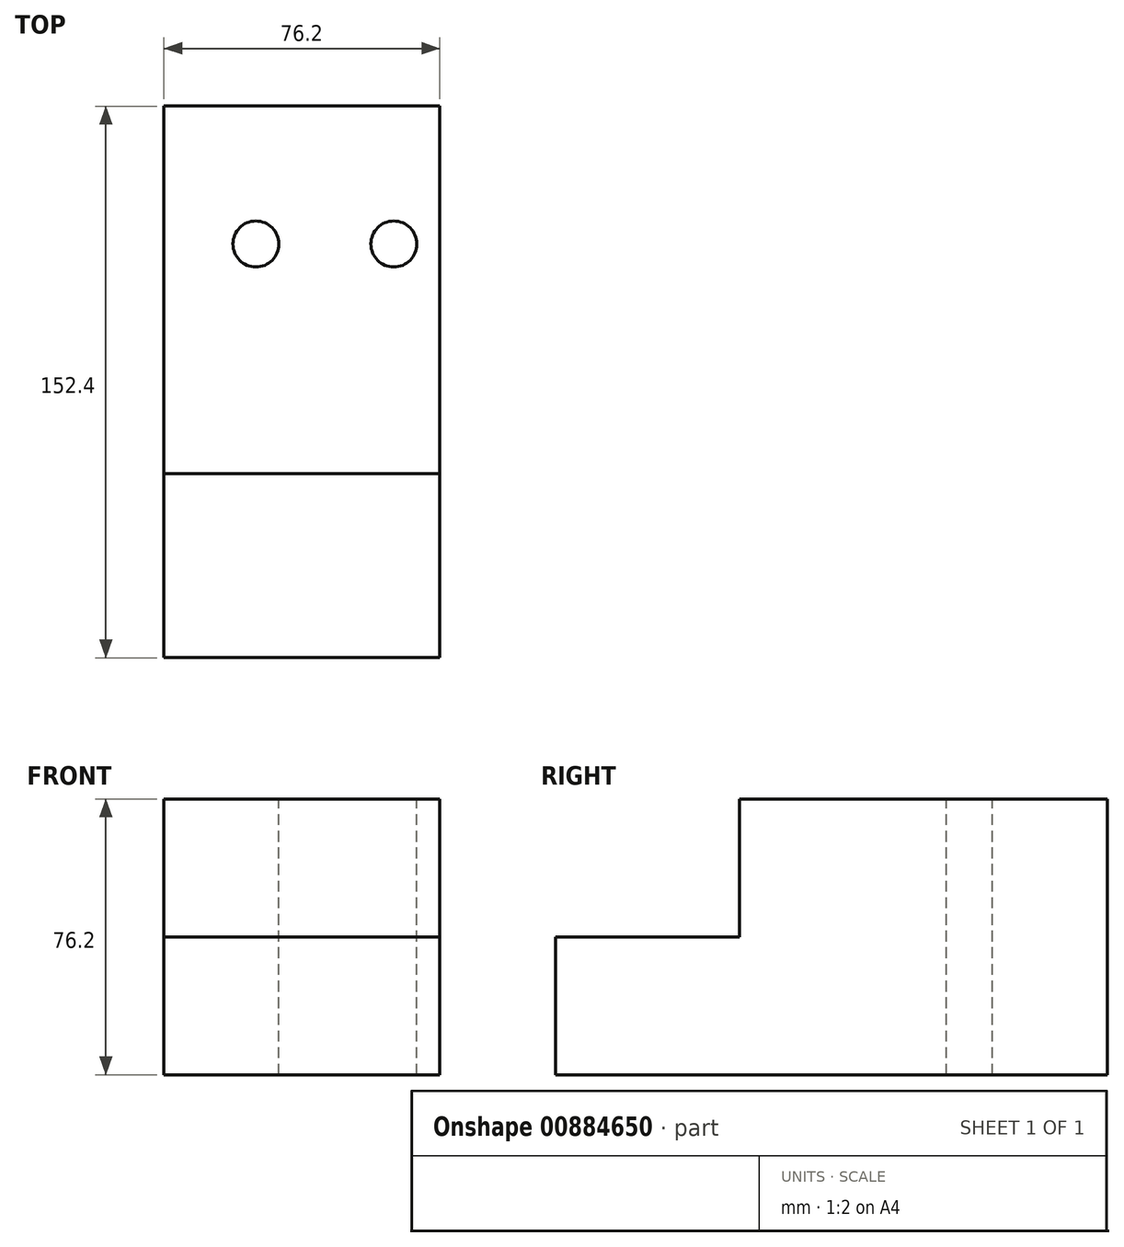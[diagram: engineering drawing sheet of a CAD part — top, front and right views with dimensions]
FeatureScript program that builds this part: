
annotation { "Feature Type Name" : "Feature", "Feature Type Description" : "" }
export const myFeature = defineFeature(function(context is Context, id is Id, definition is map)
    precondition{}
    {
        {
            var Q0;
            Q0=qCreatedBy(makeId("Top.planeOp"),FACE);
            var sketch = newSketch(context, id + "F0", { "sketchPlane" : qUnion([Q0])});
            skLineSegment(sketch, "E0.bottom", {"start": v(-31.3, 38.55) * mm, "end": v(44.9, 38.55) * mm});
            skLineSegment(sketch, "E0.top", {"start": v(-31.3, -63.05) * mm, "end": v(44.9, -63.05) * mm});
            skLineSegment(sketch, "E0.left", {"start": v(-31.3, 38.55) * mm, "end": v(-31.3, -63.05) * mm});
            skLineSegment(sketch, "E0.right", {"start": v(44.9, 38.55) * mm, "end": v(44.9, -63.05) * mm});
            skCircle(sketch, "E1", {"center": v(-5.9, 0.45) * mm, "radius": 6.35 * mm});
            skCircle(sketch, "E2", {"center": v(32.2, 0.45) * mm, "radius": 6.35 * mm});
            skSolve(sketch);
        }
        {
            var Q0;
            Q0 = qSketchRegion(id + "F0", true);
            extrude(context, id + "F1", {"entities" : qUnion([Q0]), "oppositeDirection" : true, "depth" : 76.2 * mm, "offsetDistance" : 25.4 * mm});
        }
        {
            var Q0;
            Q0=makeQuery(id+"F1.opExtrude","SWEPT_FACE",FACE,{"disambiguationData":[OSD([sQuery(id+"F0.wireOp",EDGE,"E0.top")])]});
            var sketch = newSketch(context, id + "F2", { "sketchPlane" : qUnion([Q0])});
            skLineSegment(sketch, "E3.bottom", {"start": v(-31.3, -38.1) * mm, "end": v(44.9, -38.1) * mm});
            skLineSegment(sketch, "E3.top", {"start": v(-31.3, -76.2) * mm, "end": v(44.9, -76.2) * mm});
            skLineSegment(sketch, "E3.left", {"start": v(-31.3, -38.1) * mm, "end": v(-31.3, -76.2) * mm});
            skLineSegment(sketch, "E3.right", {"start": v(44.9, -38.1) * mm, "end": v(44.9, -76.2) * mm});
            skSolve(sketch);
        }
        {
            var Q0;
            Q0 = qSketchRegion(id + "F2", true);
            extrude(context, id + "F3", {"entities" : qUnion([Q0]), "operationType" : NewBodyOperationType.ADD, "depth" : 50.8 * mm, "offsetDistance" : 25.4 * mm});
        }
    });
